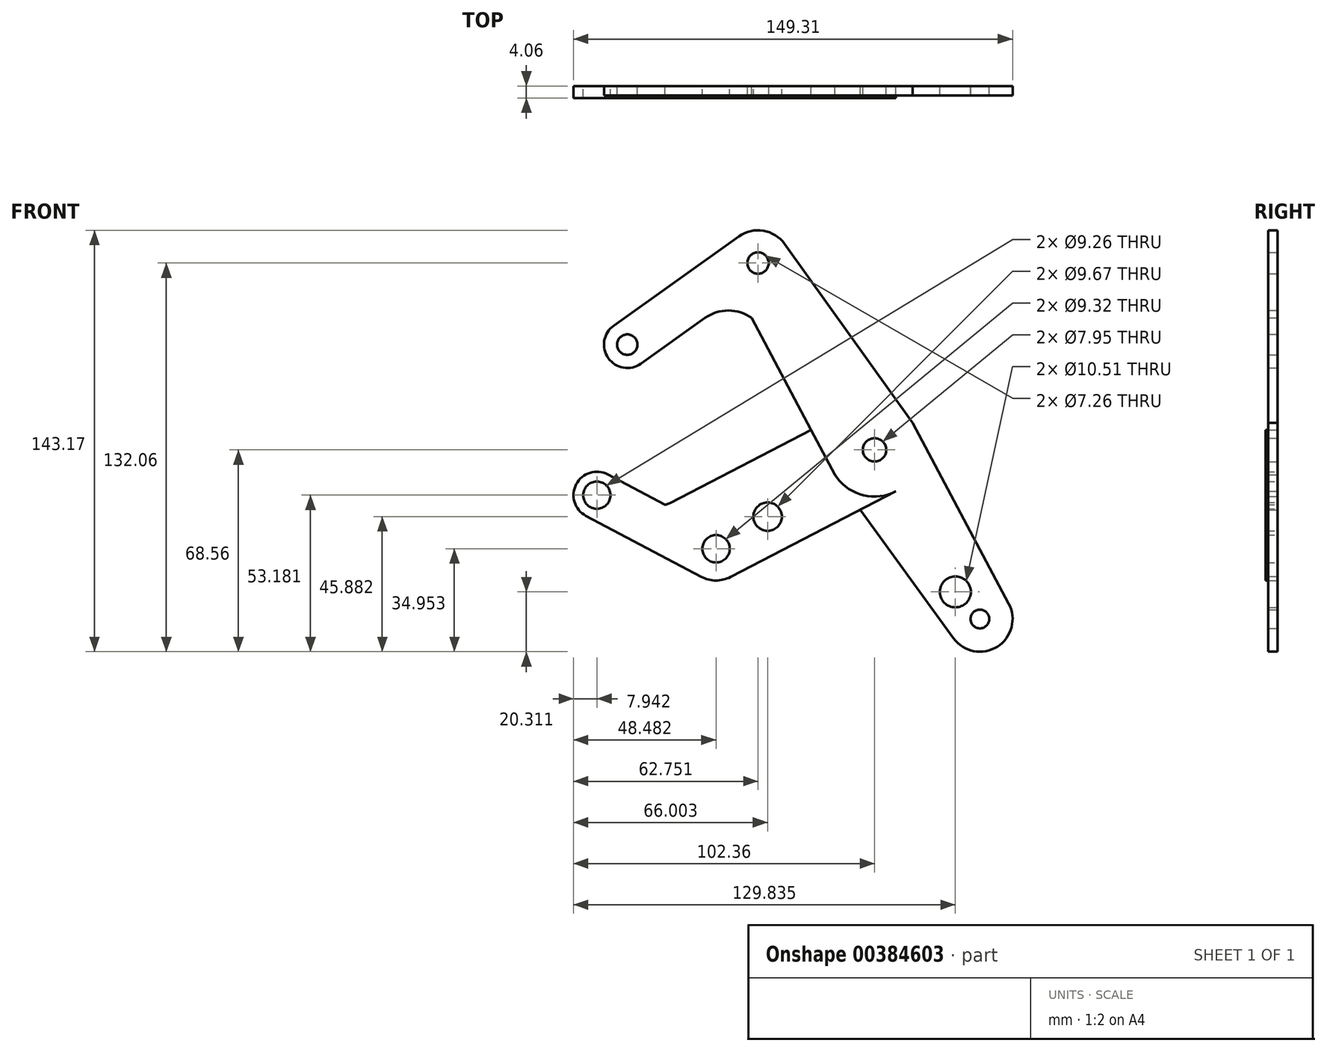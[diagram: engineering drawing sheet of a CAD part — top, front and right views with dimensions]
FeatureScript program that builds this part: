
annotation { "Feature Type Name" : "Feature", "Feature Type Description" : "" }
export const myFeature = defineFeature(function(context is Context, id is Id, definition is map)
    precondition{}
    {
        {
            var Q0;
            Q0=qCreatedBy(makeId("Front.planeOp"),FACE);
            var sketch = newSketch(context, id + "F0", { "sketchPlane" : qUnion([Q0])});
            skCircle(sketch, "E0", {"center": v(0, 0) * mm, "radius": 15.88 * mm});
            skCircle(sketch, "E1", {"center": v(0, 0) * mm, "radius": 3.98 * mm});
            skLineSegment(sketch, "E2", {"start": v(0, 0) * mm, "end": v(-39.6, 63.5) * mm, "construction": true});
            skCircle(sketch, "E3", {"center": v(-39.6, 63.5) * mm, "radius": 11.11 * mm});
            skLineSegment(sketch, "E4", {"start": v(-39.6, 63.5) * mm, "end": v(-84.06, 35.77) * mm, "construction": true});
            skCircle(sketch, "E5", {"center": v(-84.06, 35.77) * mm, "radius": 7.94 * mm});
            skCircle(sketch, "E6", {"center": v(-84.06, 35.77) * mm, "radius": 3.47 * mm});
            skCircle(sketch, "E7", {"center": v(-39.6, 63.5) * mm, "radius": 3.63 * mm});
            skLineSegment(sketch, "E8", {"start": v(0, 0) * mm, "end": v(35.83, -57.45) * mm, "construction": true});
            skCircle(sketch, "E9", {"center": v(35.83, -57.45) * mm, "radius": 11.11 * mm});
            skCircle(sketch, "E10", {"center": v(35.83, -57.45) * mm, "radius": 3.18 * mm});
            skArc(sketch, "E11", {"start": v(32.54, -46.83) * mm, "mid": v(30.4, -43.88) * mm, "end": v(26.84, -43.03) * mm});
            skArc(sketch, "E12", {"start": v(26.84, -43.03) * mm, "mid": v(24.56, -52.62) * mm, "end": v(32.54, -46.83) * mm});
            skLineSegment(sketch, "E13", {"start": v(0, 0) * mm, "end": v(-53.88, -33.6) * mm, "construction": true});
            skCircle(sketch, "E14", {"center": v(-36.36, -22.68) * mm, "radius": 4.83 * mm});
            skCircle(sketch, "E15", {"center": v(-53.88, -33.6) * mm, "radius": 10.77 * mm});
            skCircle(sketch, "E16", {"center": v(-53.88, -33.6) * mm, "radius": 4.66 * mm});
            skLineSegment(sketch, "E17", {"start": v(-53.88, -33.6) * mm, "end": v(-94.42, -15.38) * mm, "construction": true});
            skLineSegment(sketch, "E18", {"start": v(-94.42, -15.38) * mm, "end": v(-84.06, 35.77) * mm, "construction": true});
            skCircle(sketch, "E19", {"center": v(-94.42, -15.38) * mm, "radius": 7.94 * mm});
            skCircle(sketch, "E20", {"center": v(-94.42, -15.38) * mm, "radius": 4.63 * mm});
            skLineSegment(sketch, "E21", {"start": v(-88.66, 42.24) * mm, "end": v(-46.05, 72.55) * mm});
            skLineSegment(sketch, "E22", {"start": v(-79.46, 29.3) * mm, "end": v(-57.62, 44.84) * mm});
            skArc(sketch, "E23", {"start": v(-41.73, 44.84) * mm, "mid": v(-49.68, 47.38) * mm, "end": v(-57.62, 44.84) * mm});
            skLineSegment(sketch, "E24", {"start": v(-30.57, 69.97) * mm, "end": v(12.9, 9.24) * mm});
            skLineSegment(sketch, "E25", {"start": v(12.9, 9.24) * mm, "end": v(45.64, -52.22) * mm});
            skLineSegment(sketch, "E26", {"start": v(26.84, -63.98) * mm, "end": v(-13.5, -8.42) * mm});
            skLineSegment(sketch, "E27", {"start": v(-13.5, -8.42) * mm, "end": v(-41.73, 44.84) * mm});
            skLineSegment(sketch, "E28", {"start": v(-69.35, -17.99) * mm, "end": v(-21.54, 6.74) * mm});
            skPoint(sketch, "E29.visualSharp", {"position": v(-64.3, -15.38) * mm});
            skArc(sketch, "E29.filletArc", {"start": v(-71.3, -18.62) * mm, "mid": v(-70.3, -18.38) * mm, "end": v(-69.35, -17.99) * mm});
            skLineSegment(sketch, "E30", {"start": v(-98.13, -22.4) * mm, "end": v(-58.9, -43.13) * mm});
            skLineSegment(sketch, "E31", {"start": v(-48.93, -43.17) * mm, "end": v(-4.83, -20.37) * mm});
            skLineSegment(sketch, "E32", {"start": v(-71.3, -18.62) * mm, "end": v(-92.78, -7.27) * mm});
            skLineSegment(sketch, "E33.trimOffspring", {"start": v(7.3, -14.1) * mm, "end": v(8.43, -13.51) * mm});
            skLineSegment(sketch, "E34", {"start": v(-4.83, -20.37) * mm, "end": v(7.3, -14.1) * mm});
            skLineSegment(sketch, "E35", {"start": v(-21.54, 6.74) * mm, "end": v(-8.43, 13.51) * mm});
            skSolve(sketch);
        }
        {
            var Q0;
            {var subQ0=sQuery(id+"F0.wireOp",EDGE,"E21");Q0=makeQuery(id+"F0.imprint","IMPRINT",FACE,{"disambiguationData":[TD([[makeQuery(id+"F0.imprint","IMPRINT",EDGE,{"derivedFrom":subQ0}),-1.0]])]});}
            var Q1;
            {var subQ0=sQuery(id+"F0.wireOp",EDGE,"E11");Q1=makeQuery(id+"F0.imprint","IMPRINT",FACE,{"disambiguationData":[TD([[makeQuery(id+"F0.imprint","IMPRINT",EDGE,{"derivedFrom":subQ0}),-1.0]])]});}
            var Q2;
            Q2=makeQuery(id+"F0.imprint","IMPRINT",FACE,{"disambiguationData":[TD([[makeQuery(id+"F0.imprint","IMPRINT",EDGE,{"derivedFrom":sQuery(id+"F0.wireOp",EDGE,"E1")}),-1.0]])]});
            var Q3;
            Q3=makeQuery(id+"F0.imprint","IMPRINT",FACE,{"disambiguationData":[TD([[makeQuery(id+"F0.imprint","IMPRINT",EDGE,{"derivedFrom":sQuery(id+"F0.wireOp",EDGE,"E7")}),-1.0]])]});
            var Q4;
            Q4=makeQuery(id+"F0.imprint","IMPRINT",FACE,{"disambiguationData":[TD([[makeQuery(id+"F0.imprint","IMPRINT",EDGE,{"derivedFrom":sQuery(id+"F0.wireOp",EDGE,"E6")}),-1.0]])]});
            var Q5;
            Q5=makeQuery(id+"F0.imprint","IMPRINT",FACE,{"disambiguationData":[TD([[makeQuery(id+"F0.imprint","IMPRINT",EDGE,{"derivedFrom":sQuery(id+"F0.wireOp",EDGE,"E10")}),-1.0]])]});
            extrude(context, id + "F1", {"entities" : qUnion([Q0, Q1, Q2, Q3, Q4, Q5]), "depth" : 3.17 * mm});
        }
        {
            var Q0;
            {var subQ0=sQuery(id+"F0.wireOp",EDGE,"E34");Q0=makeQuery(id+"F0.imprint","IMPRINT",FACE,{"disambiguationData":[TD([[makeQuery(id+"F0.imprint","IMPRINT",EDGE,{"derivedFrom":subQ0}),1.0]])]});}
            var Q1;
            Q1=makeQuery(id+"F0.imprint","IMPRINT",FACE,{"disambiguationData":[TD([[makeQuery(id+"F0.imprint","IMPRINT",EDGE,{"derivedFrom":sQuery(id+"F0.wireOp",EDGE,"E14")}),-1.0]])]});
            var Q2;
            Q2=makeQuery(id+"F0.imprint","IMPRINT",FACE,{"disambiguationData":[TD([[makeQuery(id+"F0.imprint","IMPRINT",EDGE,{"derivedFrom":sQuery(id+"F0.wireOp",EDGE,"E20")}),-1.0]])]});
            var Q3;
            Q3=makeQuery(id+"F0.imprint","IMPRINT",FACE,{"disambiguationData":[TD([[makeQuery(id+"F0.imprint","IMPRINT",EDGE,{"derivedFrom":sQuery(id+"F0.wireOp",EDGE,"E16")}),-1.0]])]});
            extrude(context, id + "F2", {"entities" : qUnion([Q0, Q1, Q2, Q3]), "depth" : 4.06 * mm});
        }
    });
